# Revit family: Hand_Dryer-Bradley_Corp-2904-28
name_source: partatom
category: Specialty Equipment
revit_build: Autodesk Revit MEP 2012 (Build: 20110309_2315(x64)
units: mm (PartAtom-declared; Revit-internal decimal feet)

## types (2) — shared parameters
ADA Compliant = Yes
Air Opening Material = Metal - Bradley Corp - Chrome
Airspeed = 5,512 LFM
Apparent Load = 0 VA
Assembly Code = C1030200
Buy American Act = No
Default Elevation = 48"
Depth = 8 1/2"
Description = Push-Button Operated Warm Air Hand Dryer
Drying Time = 29 seconds
Effective Air Flow = 203 CFM
Free Airflow = 290 CFM
Heating Element = 1,600 W (2.15hp)
Height = 10"
Insulation = Grounding Required
Main Cover Material = Metal - Bradley Corp - Porcelain - White
Manufacturer = Bradley Corporation
MasterFormat Number = 10 28 00
MasterFormat Title = Toilet, Bath, and Laundry Accessories
Motor = 1/3hp (250W)
Noise Level at 79" = 70dB
OmniClass Table 21 Number = 21-03 10 90 40
OmniClass Table 21 Title = Toilet, Bath, and Laundry Accessories
OmniClass Table 23 Number = 23-31 25 15
OmniClass Table 23 Title = Hand and Hair Dryers
Product Tech Data URL - English = http://bradleycorp.com
RPM = 5,500
Specifications URL = http://www.bradleycorp.com
Temperature (At 4" distance 70°F) = 128°F (53°C)
URL = http://www.bradleycorp.com
Version = 2.0
Warranty Information = Sensors 1 year, motor brushes 3 years, all other components 10 years.
Width = 11 1/8"
zero-valued in all types: Percentage of Recycled Content

## per-type parameters (varying)
| type | Consumption | Frequency | Industry Standards | Nominal Power | Type Comments | Voltage |
| 2904-28 | 16 A | 60 Hz | UL 499/CSA C22.2 | 1,850 W (2.5hp) |  | 120 V |
| 2904-28CE | 10 A | 50 Hz | VDE GS/VDE EMC/CE GOST | 2,250 W (3hp) | European Certification | 240 V |

note: column(s) folded — value = type name in every type: Model

## geometry (parser evidence)
native form markers: Blend x8, Sweep x1
no freeform markers — native parametric forms only
